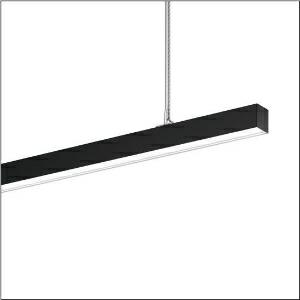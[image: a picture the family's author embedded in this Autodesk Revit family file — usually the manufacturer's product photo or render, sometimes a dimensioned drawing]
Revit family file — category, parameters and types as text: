
# Revit family: silica_21_51mx33da37bb
name_source: partatom
category: Lighting Fixtures
units: mm (PartAtom-declared; Revit-internal decimal feet)

## family parameters
Cut with Voids When Loaded = No
Host = Face
Light Source = No
Part Type = Normal
Room Calculation Point = No
Round Connector Dimension = Use Diameter
Shared = No

## types (1)
- --- (1 x LED, 5910 lm, 41.3 W, 3000K)
    Apparent Load = 41 VA
    CIE Flux Codes = 78 96 99 55 100
    Color Rendering = 80
    Color Temperature = 3000K
    Default Elevation = 1800 mm
    Description = Silica 21, office luminaire, primary optical cover: prismatic diffuser, of PMMA, CAT 2 (L<= 3000cd/m²), light emission: direct/indirect distribution, primary light characteristic: symmetric, installation type: suspended mounting, LED, rated luminous flux: 5.910lm, luminous efficacy: 143lm/W, light colour: 830, colour temperature: 3000K, control gear: DALI 2, with terminal, 3+2-pole, max. 2.5mm², mains connection: 220..240V, AC, 50/60Hz, rated input power: 41.3W, luminaire housing, of aluminium, matt jet black (RAL 9005), length: 1.204mm, width: 53mm, height: 53mm, protection rating (complete): IP20, insulation class (complete): insulation class I (protective earthing), certification: CE, permissible operating ambient temperature: 0..+35°C, standard: EN 50419, packaging unit: 1 piece
    Height = 53 mm
    Lamp = 1 x LED
    Lamp Light Flux = 5910 lm
    Lamp Power = 41.3 W
    Lamp count = 1
    Length = 1204 mm
    Luminous efficacy = 143 lm/W
    Manufacturer = Siteco
    ModVariant = No
    Model = 51MX33DA37BB
    Mounting Place = Ceiling
    Mounting Type = Pendant
    Number of Poles = 1
    OnlyDefault = Yes
    Power Factor = 1
    Product Name = Silica 21
    Product group = office luminaire | ceiling pendant
    ProductGroupID = 903
    Protection Class = Protection class I
    Protection Degree = IP 20
    RLX_Detail_Level = 1
    RLX_Emergency_Light_Flux = 0 lm
    RLX_Emergency_Type = 0
    RLX_Emergency_Type_DB = No
    RlxData = <blob elided: 26181 chars, md5=11f87898>
    Socket = socket
    Standby Power = 0 W
    System Light Flux = 5910 lm
    System Power = 41 W
    Type Comments = factory setting: luminous flux: 100 % | dim-lin: 254 | 345 mA
    Type Image = l_1335856.jpg
    URL = http://relux.com
    VarID = @adj_118879
    Voltage = 0 V
    Weight = 0.00 kg
    Width = 53 mm

## geometry (parser evidence)
native form markers: Blend x4, Sweep x10
no freeform markers — native parametric forms only
